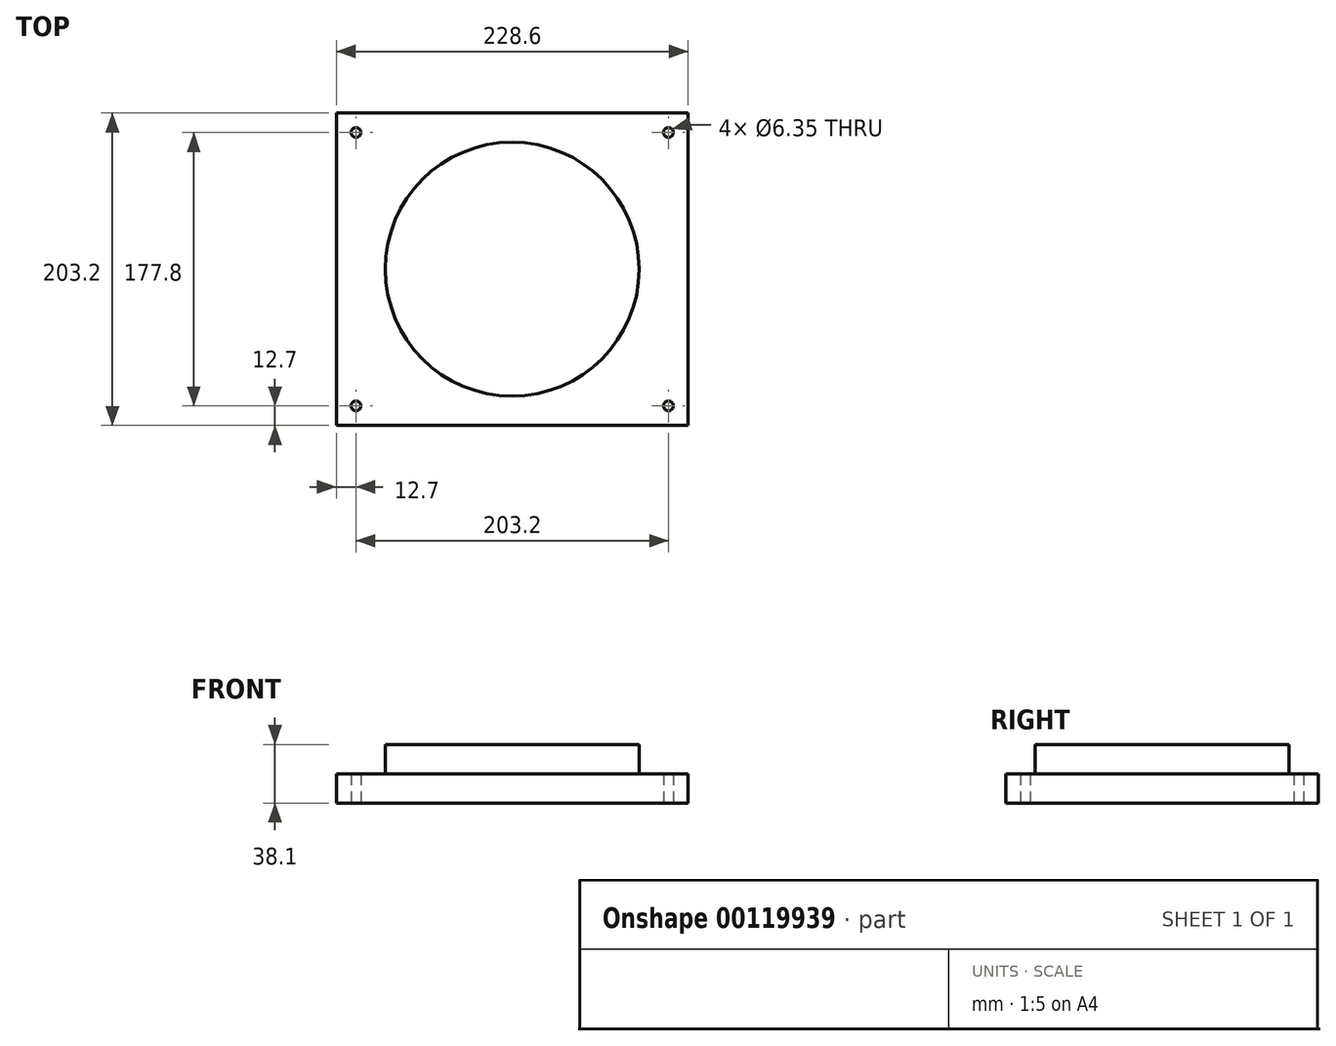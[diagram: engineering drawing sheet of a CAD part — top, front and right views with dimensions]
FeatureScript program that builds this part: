
annotation { "Feature Type Name" : "Feature", "Feature Type Description" : "" }
export const myFeature = defineFeature(function(context is Context, id is Id, definition is map)
    precondition{}
    {
        {
            var Q0;
            Q0=qCreatedBy(makeId("Top.planeOp"),FACE);
            var sketch = newSketch(context, id + "F0", { "sketchPlane" : qUnion([Q0])});
            skLineSegment(sketch, "E0.bottom", {"start": v(0, 0) * mm, "end": v(228.6, 0) * mm});
            skLineSegment(sketch, "E0.top", {"start": v(0, 203.2) * mm, "end": v(228.6, 203.2) * mm});
            skLineSegment(sketch, "E0.left", {"start": v(0, 0) * mm, "end": v(0, 203.2) * mm});
            skLineSegment(sketch, "E0.right", {"start": v(228.6, 0) * mm, "end": v(228.6, 203.2) * mm});
            skCircle(sketch, "E1", {"center": v(12.7, 190.5) * mm, "radius": 3.18 * mm});
            skCircle(sketch, "E2", {"center": v(215.9, 190.5) * mm, "radius": 3.18 * mm});
            skCircle(sketch, "E3", {"center": v(12.7, 12.7) * mm, "radius": 3.18 * mm});
            skCircle(sketch, "E4", {"center": v(215.9, 12.7) * mm, "radius": 3.18 * mm});
            skCircle(sketch, "E5", {"center": v(114.3, 101.6) * mm, "radius": 82.55 * mm});
            skSolve(sketch);
        }
        {
            var Q0;
            Q0=makeQuery(id+"F0.imprint","IMPRINT",FACE,{"disambiguationData":[TD([[makeQuery(id+"F0.imprint","IMPRINT",EDGE,{"derivedFrom":sQuery(id+"F0.wireOp",EDGE,"E5")}),1.0]])]});
            extrude(context, id + "F1", {"entities" : qUnion([Q0]), "depth" : 38.1 * mm});
        }
        {
            var Q0;
            Q0=makeQuery(id+"F0.imprint","IMPRINT",FACE,{"disambiguationData":[TD([[makeQuery(id+"F0.imprint","IMPRINT",EDGE,{"derivedFrom":sQuery(id+"F0.wireOp",EDGE,"E0.bottom")}),1.0]])]});
            extrude(context, id + "F2", {"entities" : qUnion([Q0]), "operationType" : NewBodyOperationType.ADD, "depth" : 19.05 * mm});
        }
    });
